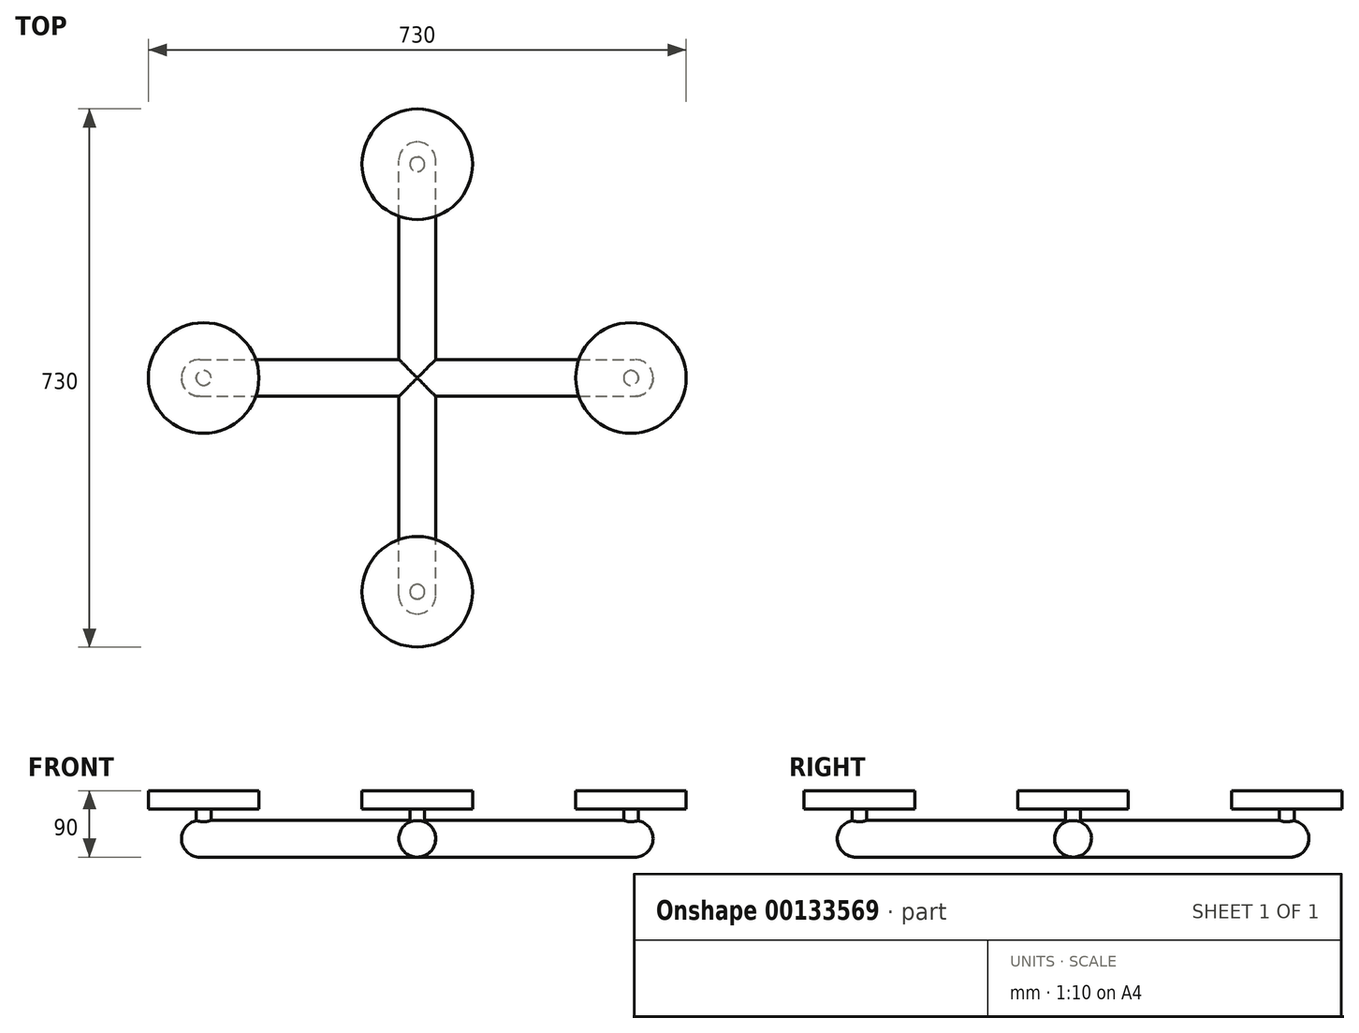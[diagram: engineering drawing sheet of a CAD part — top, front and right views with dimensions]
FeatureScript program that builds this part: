
annotation { "Feature Type Name" : "Feature", "Feature Type Description" : "" }
export const myFeature = defineFeature(function(context is Context, id is Id, definition is map)
    precondition{}
    {
        {
            var Q0;
            Q0=qCreatedBy(makeId("Front.planeOp"),FACE);
            var sketch = newSketch(context, id + "F0", { "sketchPlane" : qUnion([Q0])});
            skCircle(sketch, "E0", {"center": v(0, 0) * mm, "radius": 25 * mm});
            skLineSegment(sketch, "E1", {"start": v(0, 56.01) * mm, "end": v(0, -53.07) * mm, "construction": true});
            skLineSegment(sketch, "E2", {"start": v(0, 25) * mm, "end": v(-20.92, 25) * mm, "construction": true});
            skLineSegment(sketch, "E3", {"start": v(-20.92, 25) * mm, "end": v(25.1, 25) * mm, "construction": true});
            skSolve(sketch);
        }
        {
            var Q0;
            Q0 = qSketchRegion(id + "F0", true);
            extrude(context, id + "F1", {"entities" : qUnion([Q0]), "endBound" : BoundingType.SYMMETRIC, "depth" : 640 * mm});
        }
        {
            var Q0;
            Q0=makeQuery(id+"F1.opExtrude","SWEPT_BODY",BODY,{"disambiguationData":[OSD([sQuery(id+"F0.wireOp",EDGE,"E0")])]});
            var Q1;
            Q1=sQuery(id+"F0.wireOp",EDGE,"E1");
            circularPattern(context, id + "F2", {"operationType" : NewBodyOperationType.ADD, "entities" : qUnion([Q0]), "axis" : qUnion([Q1]), "angle" : 90 * degree, "instanceCount" : 2});
        }
        {
            var Q0;
            Q0=makeQuery(id+"F1.opExtrude","CAP_FACE",FACE,{"disambiguationData":[OSD([sQuery(id+"F0.wireOp",EDGE,"E0")])],"isStart":false});
            var Q1;
            Q1=makeQuery(id+"F2.opPattern","COPY",FACE,{"derivedFrom":makeQuery(id+"F1.opExtrude","CAP_FACE",FACE,{"disambiguationData":[OSD([sQuery(id+"F0.wireOp",EDGE,"E0")])],"isStart":true}),"instanceName":"1"});
            var Q2;
            Q2=makeQuery(id+"F1.opExtrude","CAP_EDGE",EDGE,{"disambiguationData":[OSD([sQuery(id+"F0.wireOp",EDGE,"E0")])],"isStart":true});
            var Q3;
            Q3=makeQuery(id+"F2.opPattern","COPY",EDGE,{"derivedFrom":makeQuery(id+"F1.opExtrude","CAP_EDGE",EDGE,{"disambiguationData":[OSD([sQuery(id+"F0.wireOp",EDGE,"E0")])],"isStart":false}),"instanceName":"1"});
            fillet(context, id + "F3", {"entities" : qUnion([Q0, Q1, Q2, Q3]), "radius" : 25 * mm, "tangentPropagation" : true, "allowEdgeOverflow" : false});
        }
        {
            var Q0;
            Q0=qCreatedBy(makeId("Top.planeOp"),FACE);
            var sketch = newSketch(context, id + "F4", { "sketchPlane" : qUnion([Q0])});
            skLineSegment(sketch, "E4", {"start": v(0, 0) * mm, "end": v(-290, 0) * mm, "construction": true});
            skPoint(sketch, "E5.center", {"position": v(0, 0) * mm});
            skCircle(sketch, "E6", {"center": v(-290, 0) * mm, "radius": 10 * mm});
            skLineSegment(sketch, "E7.1.0", {"start": v(0, 0) * mm, "end": v(0, -290) * mm, "construction": true});
            skLineSegment(sketch, "E7.2.0", {"start": v(0, 0) * mm, "end": v(290, 0) * mm, "construction": true});
            skLineSegment(sketch, "E7.3.0", {"start": v(0, 0) * mm, "end": v(0, 290) * mm, "construction": true});
            skLineSegment(sketch, "E7.anchor2", {"start": v(0, 0) * mm, "end": v(0, 290) * mm, "construction": true});
            skCircle(sketch, "E8.1.0", {"center": v(0, -290) * mm, "radius": 10 * mm});
            skCircle(sketch, "E8.2.0", {"center": v(290, 0) * mm, "radius": 10 * mm});
            skCircle(sketch, "E8.3.0", {"center": v(0, 290) * mm, "radius": 10 * mm});
            skSolve(sketch);
        }
        {
            var Q0;
            Q0 = qSketchRegion(id + "F4", true);
            extrude(context, id + "F5", {"entities" : qUnion([Q0]), "operationType" : NewBodyOperationType.ADD, "depth" : 40 * mm});
        }
        {
            var Q0;
            Q0=makeQuery(id+"F5.opExtrude","CAP_FACE",FACE,{"disambiguationData":[OSD([sQuery(id+"F4.wireOp",EDGE,"E6")])],"isStart":false});
            cPlane(context, id + "F6", {"entities" : qUnion([Q0]), "cplaneType" : CPlaneType.OFFSET, "offset" : 0 * mm, "width" : 150 * mm, "height" : 150 * mm});
        }
        {
            var Q0;
            Q0=qCreatedBy(id+"F6.planeOp",FACE);
            var sketch = newSketch(context, id + "F7", { "sketchPlane" : qUnion([Q0])});
            skLineSegment(sketch, "E9", {"start": v(0, 0) * mm, "end": v(-290, 0) * mm, "construction": true});
            skCircle(sketch, "E10", {"center": v(-290, 0) * mm, "radius": 75 * mm});
            skCircle(sketch, "E11.1.0", {"center": v(0, 290) * mm, "radius": 75 * mm});
            skCircle(sketch, "E11.2.0", {"center": v(290, 0) * mm, "radius": 75 * mm});
            skCircle(sketch, "E11.3.0", {"center": v(0, -290) * mm, "radius": 75 * mm});
            skPoint(sketch, "E11.center", {"position": v(0, 0) * mm});
            skLineSegment(sketch, "E11.anchor2", {"start": v(0, 0) * mm, "end": v(0, -290) * mm, "construction": true});
            skSolve(sketch);
        }
        {
            var Q0;
            Q0 = qSketchRegion(id + "F7", true);
            extrude(context, id + "F8", {"entities" : qUnion([Q0]), "operationType" : NewBodyOperationType.ADD, "depth" : 25 * mm});
        }
    });
